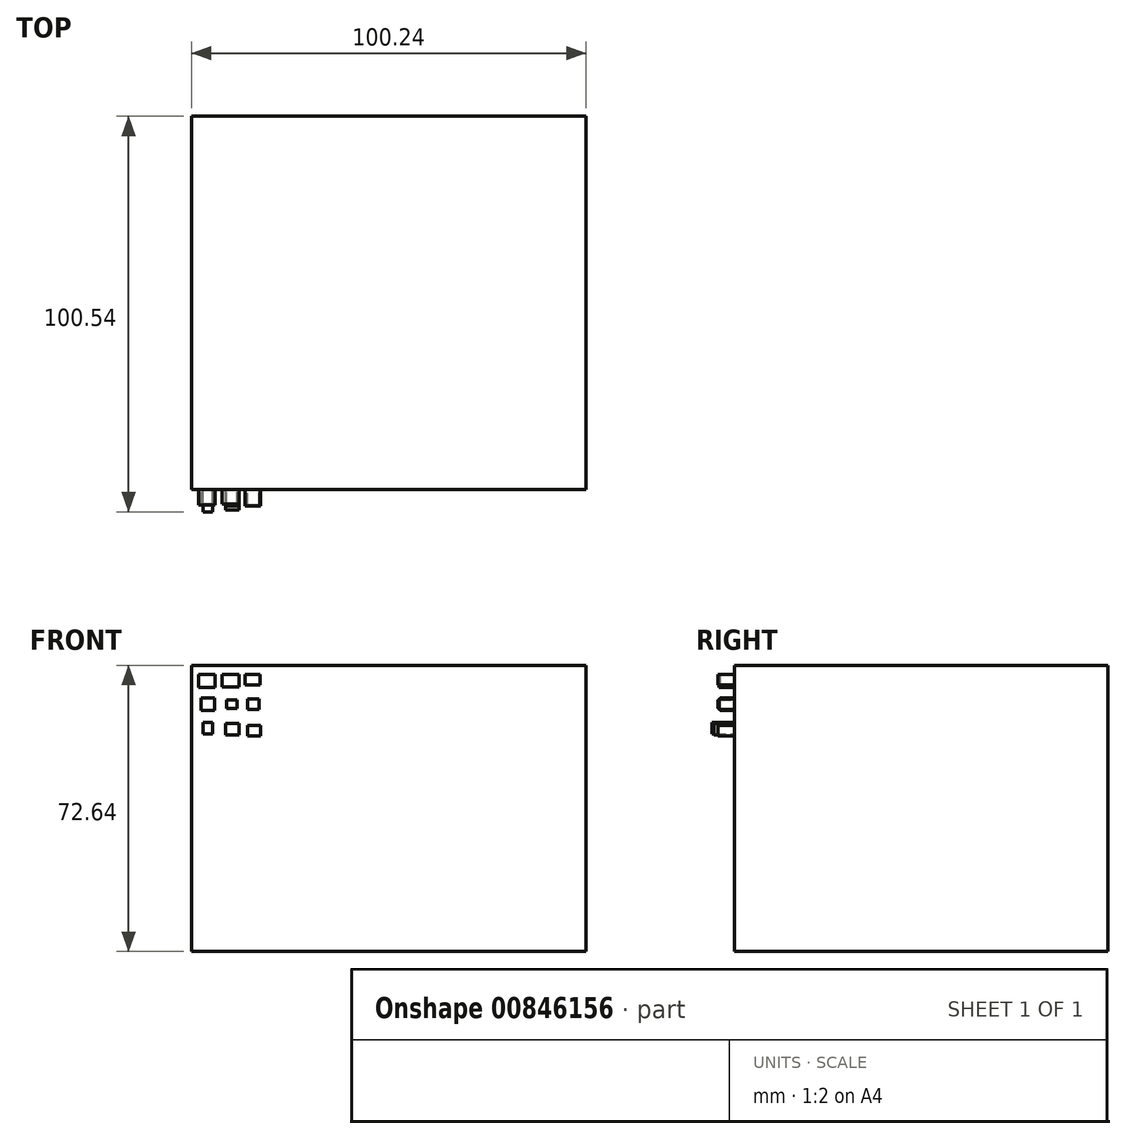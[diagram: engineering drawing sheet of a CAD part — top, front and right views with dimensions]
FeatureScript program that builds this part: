
annotation { "Feature Type Name" : "Feature", "Feature Type Description" : "" }
export const myFeature = defineFeature(function(context is Context, id is Id, definition is map)
    precondition{}
    {
        {
            var Q0;
            Q0=qCreatedBy(makeId("Top.planeOp"),FACE);
            var sketch = newSketch(context, id + "F0", { "sketchPlane" : qUnion([Q0])});
            skLineSegment(sketch, "E0.bottom", {"start": v(-50.12, 47.45) * mm, "end": v(50.12, 47.45) * mm});
            skLineSegment(sketch, "E0.top", {"start": v(-50.12, -47.45) * mm, "end": v(50.12, -47.45) * mm});
            skLineSegment(sketch, "E0.left", {"start": v(-50.12, 47.45) * mm, "end": v(-50.12, -47.45) * mm});
            skLineSegment(sketch, "E0.right", {"start": v(50.12, 47.45) * mm, "end": v(50.12, -47.45) * mm});
            skPoint(sketch, "E0.middle", {"position": v(0, 0) * mm});
            skSolve(sketch);
        }
        {
            var Q0;
            Q0 = qSketchRegion(id + "F0", true);
            extrude(context, id + "F1", {"entities" : qUnion([Q0]), "depth" : 72.64 * mm, "offsetDistance" : 25.4 * mm});
        }
        {
            var Q0;
            Q0=qCreatedBy(makeId("Front.planeOp"),FACE);
            var sketch = newSketch(context, id + "F2", { "sketchPlane" : qUnion([Q0])});
            skLineSegment(sketch, "E1.bottom", {"start": v(-48.34, 70.34) * mm, "end": v(-44.12, 70.34) * mm});
            skLineSegment(sketch, "E1.top", {"start": v(-48.34, 67) * mm, "end": v(-44.12, 67) * mm});
            skLineSegment(sketch, "E1.left", {"start": v(-48.34, 70.34) * mm, "end": v(-48.34, 67) * mm});
            skLineSegment(sketch, "E1.right", {"start": v(-44.12, 70.34) * mm, "end": v(-44.12, 67) * mm});
            skSolve(sketch);
        }
        {
            var Q0;
            Q0 = qSketchRegion(id + "F2", true);
            extrude(context, id + "F3", {"entities" : qUnion([Q0]), "operationType" : NewBodyOperationType.ADD, "depth" : 51.3 * mm, "offsetDistance" : 25.4 * mm});
        }
        {
            var Q0;
            Q0=qCreatedBy(makeId("Front.planeOp"),FACE);
            var sketch = newSketch(context, id + "F4", { "sketchPlane" : qUnion([Q0])});
            skLineSegment(sketch, "E2.bottom", {"start": v(-42.34, 70.34) * mm, "end": v(-38.12, 70.34) * mm});
            skLineSegment(sketch, "E2.top", {"start": v(-42.34, 67.23) * mm, "end": v(-38.12, 67.23) * mm});
            skLineSegment(sketch, "E2.left", {"start": v(-42.34, 70.34) * mm, "end": v(-42.34, 67.23) * mm});
            skLineSegment(sketch, "E2.right", {"start": v(-38.12, 70.34) * mm, "end": v(-38.12, 67.23) * mm});
            skSolve(sketch);
        }
        {
            var Q0;
            Q0 = qSketchRegion(id + "F4", true);
            extrude(context, id + "F5", {"entities" : qUnion([Q0]), "operationType" : NewBodyOperationType.ADD, "depth" : 51.05 * mm, "offsetDistance" : 25.4 * mm});
        }
        {
            var Q0;
            Q0=qCreatedBy(makeId("Front.planeOp"),FACE);
            var sketch = newSketch(context, id + "F6", { "sketchPlane" : qUnion([Q0])});
            skLineSegment(sketch, "E3.bottom", {"start": v(-36.56, 70.34) * mm, "end": v(-32.78, 70.34) * mm});
            skLineSegment(sketch, "E3.top", {"start": v(-36.56, 67.68) * mm, "end": v(-32.78, 67.68) * mm});
            skLineSegment(sketch, "E3.left", {"start": v(-36.56, 70.34) * mm, "end": v(-36.56, 67.68) * mm});
            skLineSegment(sketch, "E3.right", {"start": v(-32.78, 70.34) * mm, "end": v(-32.78, 67.68) * mm});
            skSolve(sketch);
        }
        {
            var Q0;
            Q0 = qSketchRegion(id + "F6", true);
            extrude(context, id + "F7", {"entities" : qUnion([Q0]), "operationType" : NewBodyOperationType.ADD, "depth" : 51.56 * mm, "offsetDistance" : 25.4 * mm});
        }
        {
            var Q0;
            Q0=qCreatedBy(makeId("Front.planeOp"),FACE);
            var sketch = newSketch(context, id + "F8", { "sketchPlane" : qUnion([Q0])});
            skLineSegment(sketch, "E4.bottom", {"start": v(-44.34, 64.34) * mm, "end": v(-47.67, 64.34) * mm});
            skLineSegment(sketch, "E4.top", {"start": v(-44.34, 61.23) * mm, "end": v(-47.67, 61.23) * mm});
            skLineSegment(sketch, "E4.left", {"start": v(-44.34, 64.34) * mm, "end": v(-44.34, 61.23) * mm});
            skLineSegment(sketch, "E4.right", {"start": v(-47.67, 64.34) * mm, "end": v(-47.67, 61.23) * mm});
            skSolve(sketch);
        }
        {
            var Q0;
            Q0 = qSketchRegion(id + "F8", true);
            extrude(context, id + "F9", {"entities" : qUnion([Q0]), "operationType" : NewBodyOperationType.ADD, "depth" : 51.05 * mm, "offsetDistance" : 25.4 * mm});
        }
        {
            var Q0;
            Q0=qCreatedBy(makeId("Front.planeOp"),FACE);
            var sketch = newSketch(context, id + "F10", { "sketchPlane" : qUnion([Q0])});
            skLineSegment(sketch, "E5.bottom", {"start": v(-38.56, 63.9) * mm, "end": v(-41.23, 63.9) * mm});
            skLineSegment(sketch, "E5.top", {"start": v(-38.56, 61.67) * mm, "end": v(-41.23, 61.67) * mm});
            skLineSegment(sketch, "E5.left", {"start": v(-38.56, 63.9) * mm, "end": v(-38.56, 61.67) * mm});
            skLineSegment(sketch, "E5.right", {"start": v(-41.23, 63.9) * mm, "end": v(-41.23, 61.67) * mm});
            skSolve(sketch);
        }
        {
            var Q0;
            Q0 = qSketchRegion(id + "F10", true);
            extrude(context, id + "F11", {"entities" : qUnion([Q0]), "operationType" : NewBodyOperationType.ADD, "depth" : 51.56 * mm, "offsetDistance" : 25.4 * mm});
        }
        {
            var Q0;
            Q0=qCreatedBy(makeId("Front.planeOp"),FACE);
            var sketch = newSketch(context, id + "F12", { "sketchPlane" : qUnion([Q0])});
            skLineSegment(sketch, "E6.bottom", {"start": v(-33, 64.12) * mm, "end": v(-35.9, 64.12) * mm});
            skLineSegment(sketch, "E6.top", {"start": v(-33, 61.45) * mm, "end": v(-35.9, 61.45) * mm});
            skLineSegment(sketch, "E6.left", {"start": v(-33, 64.12) * mm, "end": v(-33, 61.45) * mm});
            skLineSegment(sketch, "E6.right", {"start": v(-35.9, 64.12) * mm, "end": v(-35.9, 61.45) * mm});
            skSolve(sketch);
        }
        {
            var Q0;
            Q0 = qSketchRegion(id + "F12", true);
            extrude(context, id + "F13", {"entities" : qUnion([Q0]), "operationType" : NewBodyOperationType.ADD, "depth" : 51.3 * mm, "offsetDistance" : 25.4 * mm});
        }
        {
            var Q0;
            Q0=qCreatedBy(makeId("Front.planeOp"),FACE);
            var sketch = newSketch(context, id + "F14", { "sketchPlane" : qUnion([Q0])});
            skLineSegment(sketch, "E7.bottom", {"start": v(-44.78, 58.12) * mm, "end": v(-47.23, 58.12) * mm});
            skLineSegment(sketch, "E7.top", {"start": v(-44.78, 55.23) * mm, "end": v(-47.23, 55.23) * mm});
            skLineSegment(sketch, "E7.left", {"start": v(-44.78, 58.12) * mm, "end": v(-44.78, 55.23) * mm});
            skLineSegment(sketch, "E7.right", {"start": v(-47.23, 58.12) * mm, "end": v(-47.23, 55.23) * mm});
            skSolve(sketch);
        }
        {
            var Q0;
            Q0 = qSketchRegion(id + "F14", true);
            extrude(context, id + "F15", {"entities" : qUnion([Q0]), "operationType" : NewBodyOperationType.ADD, "depth" : 53.1 * mm, "offsetDistance" : 25.4 * mm});
        }
        {
            var Q0;
            Q0=qCreatedBy(makeId("Front.planeOp"),FACE);
            var sketch = newSketch(context, id + "F16", { "sketchPlane" : qUnion([Q0])});
            skLineSegment(sketch, "E8.bottom", {"start": v(-38.12, 57.9) * mm, "end": v(-41.45, 57.9) * mm});
            skLineSegment(sketch, "E8.top", {"start": v(-38.12, 55) * mm, "end": v(-41.45, 55) * mm});
            skLineSegment(sketch, "E8.left", {"start": v(-38.12, 57.9) * mm, "end": v(-38.12, 55) * mm});
            skLineSegment(sketch, "E8.right", {"start": v(-41.45, 57.9) * mm, "end": v(-41.45, 55) * mm});
            skSolve(sketch);
        }
        {
            var Q0;
            Q0 = qSketchRegion(id + "F16", true);
            extrude(context, id + "F17", {"entities" : qUnion([Q0]), "operationType" : NewBodyOperationType.ADD, "depth" : 52.58 * mm, "offsetDistance" : 25.4 * mm});
        }
        {
            var Q0;
            Q0=qCreatedBy(makeId("Front.planeOp"),FACE);
            var sketch = newSketch(context, id + "F18", { "sketchPlane" : qUnion([Q0])});
            skLineSegment(sketch, "E9.bottom", {"start": v(-32.56, 57.45) * mm, "end": v(-35.9, 57.45) * mm});
            skLineSegment(sketch, "E9.top", {"start": v(-32.56, 54.78) * mm, "end": v(-35.9, 54.78) * mm});
            skLineSegment(sketch, "E9.left", {"start": v(-32.56, 57.45) * mm, "end": v(-32.56, 54.78) * mm});
            skLineSegment(sketch, "E9.right", {"start": v(-35.9, 57.45) * mm, "end": v(-35.9, 54.78) * mm});
            skSolve(sketch);
        }
        {
            var Q0;
            Q0 = qSketchRegion(id + "F18", true);
            extrude(context, id + "F19", {"entities" : qUnion([Q0]), "operationType" : NewBodyOperationType.ADD, "depth" : 51.56 * mm, "offsetDistance" : 25.4 * mm});
        }
    });
